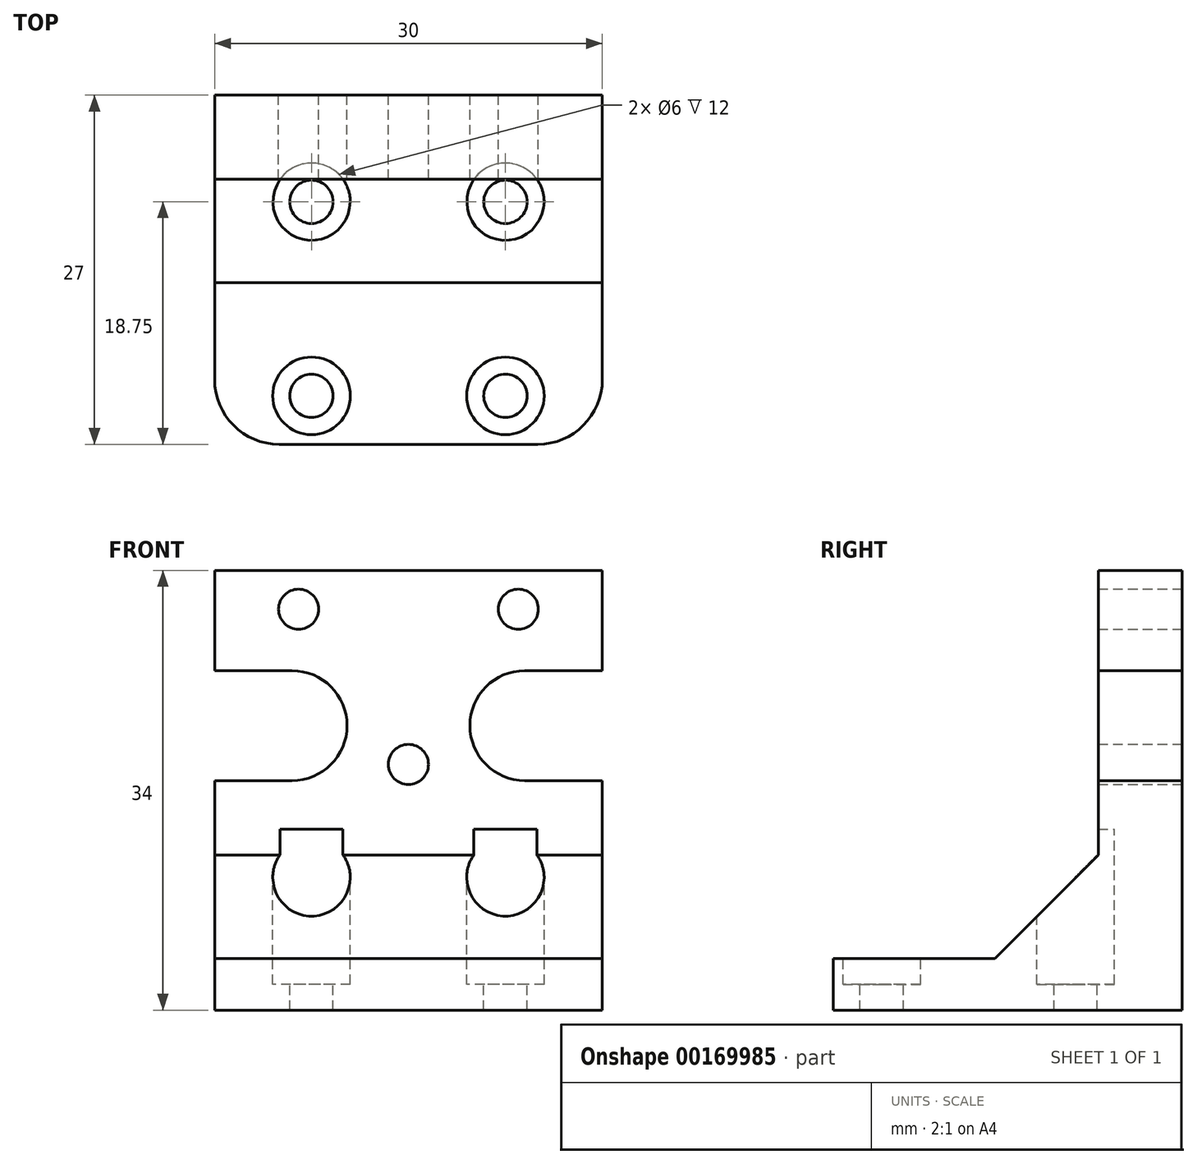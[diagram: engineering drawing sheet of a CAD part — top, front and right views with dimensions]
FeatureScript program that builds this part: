
annotation { "Feature Type Name" : "Feature", "Feature Type Description" : "" }
export const myFeature = defineFeature(function(context is Context, id is Id, definition is map)
    precondition{}
    {
        {
            var Q0;
            Q0=qCreatedBy(makeId("Top.planeOp"),FACE);
            var sketch = newSketch(context, id + "F0", { "sketchPlane" : qUnion([Q0])});
            skLineSegment(sketch, "E0.bottom", {"start": v(0, 0) * mm, "end": v(30, 0) * mm});
            skLineSegment(sketch, "E0.top", {"start": v(0, 22.5) * mm, "end": v(30, 22.5) * mm});
            skLineSegment(sketch, "E0.left", {"start": v(0, 0) * mm, "end": v(0, 22.5) * mm});
            skLineSegment(sketch, "E0.right", {"start": v(30, 0) * mm, "end": v(30, 22.5) * mm});
            skLineSegment(sketch, "E1.bottom", {"start": v(0, 27) * mm, "end": v(30, 27) * mm});
            skLineSegment(sketch, "E1.top", {"start": v(0, 20.5) * mm, "end": v(30, 20.5) * mm});
            skLineSegment(sketch, "E1.left", {"start": v(0, 27) * mm, "end": v(0, 20.5) * mm});
            skLineSegment(sketch, "E1.right", {"start": v(30, 27) * mm, "end": v(30, 20.5) * mm});
            skSolve(sketch);
        }
        {
            var Q0;
            Q0=makeQuery(id+"F0.imprint","IMPRINT",FACE,{"disambiguationData":[TD([[makeQuery(id+"F0.imprint","IMPRINT",EDGE,{"derivedFrom":sQuery(id+"F0.wireOp",EDGE,"E0.bottom")}),1.0]])]});
            var Q1;
            {var subQ0=sQuery(id+"F0.wireOp",EDGE,"E0.top");Q1=makeQuery(id+"F0.imprint","IMPRINT",FACE,{"disambiguationData":[TD([[makeQuery(id+"F0.imprint","IMPRINT",EDGE,{"derivedFrom":subQ0}),-1.0]])]});}
            extrude(context, id + "F1", {"entities" : qUnion([Q0, Q1]), "depth" : 4 * mm});
        }
        {
            var Q0;
            Q0=makeQuery(id+"F0.imprint","IMPRINT",FACE,{"disambiguationData":[TD([[makeQuery(id+"F0.imprint","IMPRINT",EDGE,{"derivedFrom":sQuery(id+"F0.wireOp",EDGE,"E0.top")}),1.0]])]});
            var Q1;
            {var subQ0=sQuery(id+"F0.wireOp",EDGE,"E0.top");Q1=makeQuery(id+"F0.imprint","IMPRINT",FACE,{"disambiguationData":[TD([[makeQuery(id+"F0.imprint","IMPRINT",EDGE,{"derivedFrom":subQ0}),-1.0]])]});}
            extrude(context, id + "F2", {"entities" : qUnion([Q0, Q1]), "operationType" : NewBodyOperationType.ADD, "depth" : 34 * mm});
        }
        {
            var Q0;
            Q0=makeQuery(id+"F1.opExtrude","CAP_FACE",FACE,{"disambiguationData":[OSD([sQuery(id+"F0.wireOp",EDGE,"E0.bottom"),sQuery(id+"F0.wireOp",EDGE,"E0.top"),sQuery(id+"F0.wireOp",EDGE,"E0.left"),sQuery(id+"F0.wireOp",EDGE,"E0.right")])],"isStart":false});
            var sketch = newSketch(context, id + "F3", { "sketchPlane" : qUnion([Q0])});
            skCircle(sketch, "E2", {"center": v(7.5, 18.75) * mm, "radius": 1.68 * mm});
            skCircle(sketch, "E3", {"center": v(22.5, 18.75) * mm, "radius": 1.68 * mm});
            skCircle(sketch, "E4", {"center": v(7.5, 3.75) * mm, "radius": 1.68 * mm});
            skCircle(sketch, "E5", {"center": v(22.5, 3.75) * mm, "radius": 1.68 * mm});
            skLineSegment(sketch, "E6", {"start": v(22.5, 3.75) * mm, "end": v(30, 3.75) * mm});
            skCircle(sketch, "E7", {"center": v(7.5, 18.75) * mm, "radius": 3 * mm});
            skCircle(sketch, "E8", {"center": v(22.5, 18.75) * mm, "radius": 3 * mm});
            skCircle(sketch, "E9", {"center": v(7.5, 3.75) * mm, "radius": 3 * mm});
            skCircle(sketch, "E10", {"center": v(22.5, 3.75) * mm, "radius": 3 * mm});
            skSolve(sketch);
        }
        {
            var Q0;
            Q0=makeQuery(id+"F3.imprint","IMPRINT",FACE,{"disambiguationData":[TD([[makeQuery(id+"F3.imprint","IMPRINT",EDGE,{"derivedFrom":sQuery(id+"F3.wireOp",EDGE,"E2")}),1.0]])]});
            var Q1;
            Q1=makeQuery(id+"F3.imprint","IMPRINT",FACE,{"disambiguationData":[TD([[makeQuery(id+"F3.imprint","IMPRINT",EDGE,{"derivedFrom":sQuery(id+"F3.wireOp",EDGE,"E3")}),1.0]])]});
            var Q2;
            Q2=makeQuery(id+"F3.imprint","IMPRINT",FACE,{"disambiguationData":[TD([[makeQuery(id+"F3.imprint","IMPRINT",EDGE,{"derivedFrom":sQuery(id+"F3.wireOp",EDGE,"E5")}),1.0]])]});
            var Q3;
            Q3=makeQuery(id+"F3.imprint","IMPRINT",FACE,{"disambiguationData":[TD([[makeQuery(id+"F3.imprint","IMPRINT",EDGE,{"derivedFrom":sQuery(id+"F3.wireOp",EDGE,"E4")}),1.0]])]});
            extrude(context, id + "F4", {"entities" : qUnion([Q0, Q1, Q2, Q3]), "operationType" : NewBodyOperationType.REMOVE, "oppositeDirection" : true, "depth" : 25 * mm});
        }
        {
            var Q0;
            Q0=makeQuery(id+"F3.imprint","IMPRINT",FACE,{"disambiguationData":[TD([[makeQuery(id+"F3.imprint","IMPRINT",EDGE,{"derivedFrom":sQuery(id+"F3.wireOp",EDGE,"E2")}),-1.0]])]});
            var Q1;
            Q1=makeQuery(id+"F3.imprint","IMPRINT",FACE,{"disambiguationData":[TD([[makeQuery(id+"F3.imprint","IMPRINT",EDGE,{"derivedFrom":sQuery(id+"F3.wireOp",EDGE,"E3")}),-1.0]])]});
            var Q2;
            Q2=makeQuery(id+"F3.imprint","IMPRINT",FACE,{"disambiguationData":[TD([[makeQuery(id+"F3.imprint","IMPRINT",EDGE,{"derivedFrom":sQuery(id+"F3.wireOp",EDGE,"E5")}),-1.0]])]});
            var Q3;
            Q3=makeQuery(id+"F3.imprint","IMPRINT",FACE,{"disambiguationData":[TD([[makeQuery(id+"F3.imprint","IMPRINT",EDGE,{"derivedFrom":sQuery(id+"F3.wireOp",EDGE,"E4")}),-1.0]])]});
            var Q4;
            {var subQ0=sQuery(id+"F3.wireOp",EDGE,"E7");var subQ1=makeQuery(id+"F2.boolean.opBoolean","INTERSECT",EDGE,{"derivedFrom":[makeQuery(id+"F1.opExtrude","CAP_FACE",FACE,{"disambiguationData":[OSD([sQuery(id+"F0.wireOp",EDGE,"E0.bottom"),sQuery(id+"F0.wireOp",EDGE,"E0.left"),sQuery(id+"F0.wireOp",EDGE,"E0.right"),sQuery(id+"F0.wireOp",EDGE,"E0.top"),sQuery(id+"F0.wireOp",EDGE,"E1.left"),sQuery(id+"F0.wireOp",EDGE,"E1.right")])],"isStart":false}),makeQuery(id+"F2.opExtrude","SWEPT_FACE",FACE,{"disambiguationData":[OSD([sQuery(id+"F0.wireOp",EDGE,"E1.top")])]})]});var subQ2=makeQuery(id+"F3.imprint","INTERSECT",VERTEX,{"disambiguationData":[OD(0.0)],"derivedFrom":[subQ1,subQ0]});Q4=makeQuery(id+"F3.imprint","IMPRINT",FACE,{"disambiguationData":[TD([[makeQuery(id+"F3.imprint","IMPRINT",EDGE,{"disambiguationData":[TD([[subQ2,1.0]])],"derivedFrom":subQ0}),1.0]])]});}
            var Q5;
            {var subQ0=sQuery(id+"F3.wireOp",EDGE,"E8");var subQ1=makeQuery(id+"F2.boolean.opBoolean","INTERSECT",EDGE,{"derivedFrom":[makeQuery(id+"F1.opExtrude","CAP_FACE",FACE,{"disambiguationData":[OSD([sQuery(id+"F0.wireOp",EDGE,"E0.bottom"),sQuery(id+"F0.wireOp",EDGE,"E0.left"),sQuery(id+"F0.wireOp",EDGE,"E0.right"),sQuery(id+"F0.wireOp",EDGE,"E0.top"),sQuery(id+"F0.wireOp",EDGE,"E1.left"),sQuery(id+"F0.wireOp",EDGE,"E1.right")])],"isStart":false}),makeQuery(id+"F2.opExtrude","SWEPT_FACE",FACE,{"disambiguationData":[OSD([sQuery(id+"F0.wireOp",EDGE,"E1.top")])]})]});var subQ2=makeQuery(id+"F3.imprint","INTERSECT",VERTEX,{"disambiguationData":[OD(0.0)],"derivedFrom":[subQ1,subQ0]});Q5=makeQuery(id+"F3.imprint","IMPRINT",FACE,{"disambiguationData":[TD([[makeQuery(id+"F3.imprint","IMPRINT",EDGE,{"disambiguationData":[TD([[subQ2,-1.0]])],"derivedFrom":subQ0}),1.0]])]});}
            extrude(context, id + "F5", {"entities" : qUnion([Q0, Q1, Q2, Q3, Q4, Q5]), "operationType" : NewBodyOperationType.REMOVE, "oppositeDirection" : true, "depth" : 2 * mm});
        }
        {
            var Q0;
            {var subQ0=sQuery(id+"F3.wireOp",EDGE,"E7");var subQ1=makeQuery(id+"F2.boolean.opBoolean","INTERSECT",EDGE,{"derivedFrom":[makeQuery(id+"F1.opExtrude","CAP_FACE",FACE,{"disambiguationData":[OSD([sQuery(id+"F0.wireOp",EDGE,"E0.bottom"),sQuery(id+"F0.wireOp",EDGE,"E0.left"),sQuery(id+"F0.wireOp",EDGE,"E0.right"),sQuery(id+"F0.wireOp",EDGE,"E0.top"),sQuery(id+"F0.wireOp",EDGE,"E1.left"),sQuery(id+"F0.wireOp",EDGE,"E1.right")])],"isStart":false}),makeQuery(id+"F2.opExtrude","SWEPT_FACE",FACE,{"disambiguationData":[OSD([sQuery(id+"F0.wireOp",EDGE,"E1.top")])]})]});var subQ2=makeQuery(id+"F3.imprint","INTERSECT",VERTEX,{"disambiguationData":[OD(0.0)],"derivedFrom":[subQ1,subQ0]});Q0=makeQuery(id+"F3.imprint","IMPRINT",FACE,{"disambiguationData":[TD([[makeQuery(id+"F3.imprint","IMPRINT",EDGE,{"disambiguationData":[TD([[subQ2,1.0]])],"derivedFrom":subQ0}),1.0]])]});}
            var Q1;
            Q1=makeQuery(id+"F3.imprint","IMPRINT",FACE,{"disambiguationData":[TD([[makeQuery(id+"F3.imprint","IMPRINT",EDGE,{"derivedFrom":sQuery(id+"F3.wireOp",EDGE,"E2")}),-1.0]])]});
            var Q2;
            {var subQ0=sQuery(id+"F3.wireOp",EDGE,"E8");var subQ1=makeQuery(id+"F2.boolean.opBoolean","INTERSECT",EDGE,{"derivedFrom":[makeQuery(id+"F1.opExtrude","CAP_FACE",FACE,{"disambiguationData":[OSD([sQuery(id+"F0.wireOp",EDGE,"E0.bottom"),sQuery(id+"F0.wireOp",EDGE,"E0.left"),sQuery(id+"F0.wireOp",EDGE,"E0.right"),sQuery(id+"F0.wireOp",EDGE,"E0.top"),sQuery(id+"F0.wireOp",EDGE,"E1.left"),sQuery(id+"F0.wireOp",EDGE,"E1.right")])],"isStart":false}),makeQuery(id+"F2.opExtrude","SWEPT_FACE",FACE,{"disambiguationData":[OSD([sQuery(id+"F0.wireOp",EDGE,"E1.top")])]})]});var subQ2=makeQuery(id+"F3.imprint","INTERSECT",VERTEX,{"disambiguationData":[OD(0.0)],"derivedFrom":[subQ1,subQ0]});Q2=makeQuery(id+"F3.imprint","IMPRINT",FACE,{"disambiguationData":[TD([[makeQuery(id+"F3.imprint","IMPRINT",EDGE,{"disambiguationData":[TD([[subQ2,-1.0]])],"derivedFrom":subQ0}),1.0]])]});}
            var Q3;
            Q3=makeQuery(id+"F3.imprint","IMPRINT",FACE,{"disambiguationData":[TD([[makeQuery(id+"F3.imprint","IMPRINT",EDGE,{"derivedFrom":sQuery(id+"F3.wireOp",EDGE,"E3")}),-1.0]])]});
            var Q4;
            Q4=makeQuery(id+"F2.opExtrude","CAP_FACE",FACE,{"disambiguationData":[OSD([sQuery(id+"F0.wireOp",EDGE,"E1.bottom"),sQuery(id+"F0.wireOp",EDGE,"E1.top"),sQuery(id+"F0.wireOp",EDGE,"E1.left"),sQuery(id+"F0.wireOp",EDGE,"E1.right")])],"isStart":false});
            extrude(context, id + "F6", {"entities" : qUnion([Q0, Q1, Q2, Q3]), "operationType" : NewBodyOperationType.REMOVE, "endBoundEntityFace" : qUnion([Q4]), "depth" : 10 * mm});
        }
        {
            var Q0;
            Q0=makeQuery(id+"F1.opExtrude","SWEPT_EDGE",EDGE,{"disambiguationData":[OSD([sQuery(id+"F0.wireOp",EDGE,"E0.bottom"),sQuery(id+"F0.wireOp",EDGE,"E0.left")])]});
            var Q1;
            Q1=makeQuery(id+"F1.opExtrude","SWEPT_EDGE",EDGE,{"disambiguationData":[OSD([sQuery(id+"F0.wireOp",EDGE,"E0.bottom"),sQuery(id+"F0.wireOp",EDGE,"E0.right")])]});
            var Q2;
            Q2=makeQuery(id+"F1.opExtrude","SWEPT_EDGE",EDGE,{"disambiguationData":[OSD([sQuery(id+"F0.wireOp",EDGE,"E0.top"),sQuery(id+"F0.wireOp",EDGE,"E0.right")])]});
            var Q3;
            Q3=makeQuery(id+"F1.opExtrude","SWEPT_EDGE",EDGE,{"disambiguationData":[OSD([sQuery(id+"F0.wireOp",EDGE,"E0.top"),sQuery(id+"F0.wireOp",EDGE,"E0.left")])]});
            fillet(context, id + "F7", {"entities" : qUnion([Q0, Q1, Q2, Q3]), "radius" : 5 * mm, "tangentPropagation" : true, "allowEdgeOverflow" : false});
        }
        {
            var Q0;
            Q0=makeQuery(id+"F2.opExtrude","SWEPT_FACE",FACE,{"disambiguationData":[OSD([sQuery(id+"F0.wireOp",EDGE,"E1.bottom")])]});
            var sketch = newSketch(context, id + "F8", { "sketchPlane" : qUnion([Q0])});
            skCircle(sketch, "E11", {"center": v(-23.5, 31) * mm, "radius": 1.55 * mm});
            skCircle(sketch, "E12", {"center": v(-6.5, 31) * mm, "radius": 1.55 * mm});
            skCircle(sketch, "E13", {"center": v(-15, 19) * mm, "radius": 1.55 * mm});
            skCircle(sketch, "E14", {"center": v(-24, 22) * mm, "radius": 4.25 * mm});
            skCircle(sketch, "E15", {"center": v(-6, 22) * mm, "radius": 4.25 * mm});
            skSolve(sketch);
        }
        {
            var Q0;
            Q0=makeQuery(id+"F8.imprint","IMPRINT",FACE,{"disambiguationData":[TD([[makeQuery(id+"F8.imprint","IMPRINT",EDGE,{"derivedFrom":sQuery(id+"F8.wireOp",EDGE,"E14")}),1.0]])]});
            var Q1;
            Q1=makeQuery(id+"F8.imprint","IMPRINT",FACE,{"disambiguationData":[TD([[makeQuery(id+"F8.imprint","IMPRINT",EDGE,{"derivedFrom":sQuery(id+"F8.wireOp",EDGE,"E11")}),1.0]])]});
            var Q2;
            Q2=makeQuery(id+"F8.imprint","IMPRINT",FACE,{"disambiguationData":[TD([[makeQuery(id+"F8.imprint","IMPRINT",EDGE,{"derivedFrom":sQuery(id+"F8.wireOp",EDGE,"E12")}),1.0]])]});
            var Q3;
            Q3=makeQuery(id+"F8.imprint","IMPRINT",FACE,{"disambiguationData":[TD([[makeQuery(id+"F8.imprint","IMPRINT",EDGE,{"derivedFrom":sQuery(id+"F8.wireOp",EDGE,"E15")}),1.0]])]});
            var Q4;
            Q4=makeQuery(id+"F8.imprint","IMPRINT",FACE,{"disambiguationData":[TD([[makeQuery(id+"F8.imprint","IMPRINT",EDGE,{"derivedFrom":sQuery(id+"F8.wireOp",EDGE,"E13")}),1.0]])]});
            extrude(context, id + "F9", {"entities" : qUnion([Q0, Q1, Q2, Q3, Q4]), "operationType" : NewBodyOperationType.REMOVE, "oppositeDirection" : true, "depth" : 7 * mm});
        }
        {
            var Q0;
            {var subQ0=sQuery(id+"F0.wireOp",EDGE,"E1.left");var subQ1=sQuery(id+"F3.wireOp",EDGE,"E7");var subQ2=makeQuery(id+"F2.opExtrude","SWEPT_FACE",FACE,{"disambiguationData":[OSD([sQuery(id+"F0.wireOp",EDGE,"E1.top")])]});var subQ3=sQuery(id+"F0.wireOp",EDGE,"E0.left");var subQ4=makeQuery(id+"F1.opExtrude","CAP_FACE",FACE,{"disambiguationData":[OSD([sQuery(id+"F0.wireOp",EDGE,"E0.bottom"),subQ3,sQuery(id+"F0.wireOp",EDGE,"E0.right"),sQuery(id+"F0.wireOp",EDGE,"E0.top"),subQ0,sQuery(id+"F0.wireOp",EDGE,"E1.right")])],"isStart":false});Q0=makeQuery(id+"F5.boolean.opBoolean","SPLIT",EDGE,{"disambiguationData":[TD([subQ4,makeQuery(id+"F1.opExtrude","SWEPT_FACE",FACE,{"disambiguationData":[OSD([subQ3,subQ0])]}),subQ2,makeQuery(id+"F2.opExtrude","SWEPT_FACE",FACE,{"disambiguationData":[OSD([subQ0])]}),makeQuery(id+"F5.opExtrude","CAP_FACE",FACE,{"disambiguationData":[OSD([sQuery(id+"F3.wireOp",EDGE,"E2"),subQ1])],"isStart":true}),makeQuery(id+"F5.opExtrude","SWEPT_FACE",FACE,{"disambiguationData":[OSD([subQ1])]})])],"derivedFrom":makeQuery(id+"F2.boolean.opBoolean","INTERSECT",EDGE,{"derivedFrom":[subQ4,subQ2]})});}
            var Q1;
            {var subQ0=sQuery(id+"F3.wireOp",EDGE,"E8");var subQ1=sQuery(id+"F3.wireOp",EDGE,"E7");var subQ2=makeQuery(id+"F2.opExtrude","SWEPT_FACE",FACE,{"disambiguationData":[OSD([sQuery(id+"F0.wireOp",EDGE,"E1.top")])]});var subQ3=makeQuery(id+"F1.opExtrude","CAP_FACE",FACE,{"disambiguationData":[OSD([sQuery(id+"F0.wireOp",EDGE,"E0.bottom"),sQuery(id+"F0.wireOp",EDGE,"E0.left"),sQuery(id+"F0.wireOp",EDGE,"E0.right"),sQuery(id+"F0.wireOp",EDGE,"E0.top"),sQuery(id+"F0.wireOp",EDGE,"E1.left"),sQuery(id+"F0.wireOp",EDGE,"E1.right")])],"isStart":false});Q1=makeQuery(id+"F5.boolean.opBoolean","SPLIT",EDGE,{"disambiguationData":[TD([subQ3,subQ2,makeQuery(id+"F5.opExtrude","CAP_FACE",FACE,{"disambiguationData":[OSD([sQuery(id+"F3.wireOp",EDGE,"E2"),subQ1])],"isStart":true}),makeQuery(id+"F5.opExtrude","CAP_FACE",FACE,{"disambiguationData":[OSD([sQuery(id+"F3.wireOp",EDGE,"E3"),subQ0])],"isStart":true}),makeQuery(id+"F5.opExtrude","SWEPT_FACE",FACE,{"disambiguationData":[OSD([subQ1])]}),makeQuery(id+"F5.opExtrude","SWEPT_FACE",FACE,{"disambiguationData":[OSD([subQ0])]})])],"derivedFrom":makeQuery(id+"F2.boolean.opBoolean","INTERSECT",EDGE,{"derivedFrom":[subQ3,subQ2]})});}
            var Q2;
            {var subQ0=sQuery(id+"F0.wireOp",EDGE,"E1.right");var subQ1=sQuery(id+"F3.wireOp",EDGE,"E8");var subQ2=makeQuery(id+"F2.opExtrude","SWEPT_FACE",FACE,{"disambiguationData":[OSD([sQuery(id+"F0.wireOp",EDGE,"E1.top")])]});var subQ3=sQuery(id+"F0.wireOp",EDGE,"E0.right");var subQ4=makeQuery(id+"F1.opExtrude","CAP_FACE",FACE,{"disambiguationData":[OSD([sQuery(id+"F0.wireOp",EDGE,"E0.bottom"),sQuery(id+"F0.wireOp",EDGE,"E0.left"),subQ3,sQuery(id+"F0.wireOp",EDGE,"E0.top"),sQuery(id+"F0.wireOp",EDGE,"E1.left"),subQ0])],"isStart":false});Q2=makeQuery(id+"F5.boolean.opBoolean","SPLIT",EDGE,{"disambiguationData":[TD([subQ4,makeQuery(id+"F1.opExtrude","SWEPT_FACE",FACE,{"disambiguationData":[OSD([subQ3,subQ0])]}),subQ2,makeQuery(id+"F2.opExtrude","SWEPT_FACE",FACE,{"disambiguationData":[OSD([subQ0])]}),makeQuery(id+"F5.opExtrude","CAP_FACE",FACE,{"disambiguationData":[OSD([sQuery(id+"F3.wireOp",EDGE,"E3"),subQ1])],"isStart":true}),makeQuery(id+"F5.opExtrude","SWEPT_FACE",FACE,{"disambiguationData":[OSD([subQ1])]})])],"derivedFrom":makeQuery(id+"F2.boolean.opBoolean","INTERSECT",EDGE,{"derivedFrom":[subQ4,subQ2]})});}
            chamfer(context, id + "F10", {"entities" : qUnion([Q0, Q1, Q2]), "width" : 8 * mm, "tangentPropagation" : true});
        }
        {
            var Q0;
            Q0=makeQuery(id+"F2.opExtrude","SWEPT_FACE",FACE,{"disambiguationData":[OSD([sQuery(id+"F0.wireOp",EDGE,"E1.bottom")])]});
            var sketch = newSketch(context, id + "F11", { "sketchPlane" : qUnion([Q0])});
            skLineSegment(sketch, "E16", {"start": v(-6, 22) * mm, "end": v(-6, 26.25) * mm});
            skLineSegment(sketch, "E17", {"start": v(-6, 26.25) * mm, "end": v(0, 26.25) * mm});
            skLineSegment(sketch, "E18", {"start": v(-6, 22) * mm, "end": v(-6, 17.75) * mm});
            skLineSegment(sketch, "E19", {"start": v(-6, 17.75) * mm, "end": v(0, 17.75) * mm});
            skLineSegment(sketch, "E20", {"start": v(0, 17.75) * mm, "end": v(0, 26.25) * mm});
            skLineSegment(sketch, "E21", {"start": v(-15, 34) * mm, "end": v(-15, 10.06) * mm});
            skLineSegment(sketch, "E22.MirrorCS", {"start": v(-24, 26.25) * mm, "end": v(-30, 26.25) * mm});
            skLineSegment(sketch, "E23.MirrorCS", {"start": v(-30, 17.75) * mm, "end": v(-30, 26.25) * mm});
            skLineSegment(sketch, "E24.MirrorCS", {"start": v(-24, 17.75) * mm, "end": v(-30, 17.75) * mm});
            skLineSegment(sketch, "E25.MirrorCS", {"start": v(-24, 22) * mm, "end": v(-24, 17.75) * mm});
            skLineSegment(sketch, "E26.MirrorCS", {"start": v(-24, 22) * mm, "end": v(-24, 26.25) * mm});
            skSolve(sketch);
        }
        {
            var Q0;
            {var subQ0=sQuery(id+"F11.wireOp",EDGE,"E17");Q0=makeQuery(id+"F11.imprint","IMPRINT",FACE,{"disambiguationData":[TD([[makeQuery(id+"F11.imprint","IMPRINT",EDGE,{"derivedFrom":subQ0}),-1.0]])]});}
            var Q1;
            {var subQ0=sQuery(id+"F11.wireOp",EDGE,"E22.MirrorCS");Q1=makeQuery(id+"F11.imprint","IMPRINT",FACE,{"disambiguationData":[TD([[makeQuery(id+"F11.imprint","IMPRINT",EDGE,{"derivedFrom":subQ0}),1.0]])]});}
            extrude(context, id + "F12", {"entities" : qUnion([Q0, Q1]), "operationType" : NewBodyOperationType.REMOVE, "endBound" : BoundingType.UP_TO_NEXT, "oppositeDirection" : true, "depth" : 25 * mm});
        }
    });
